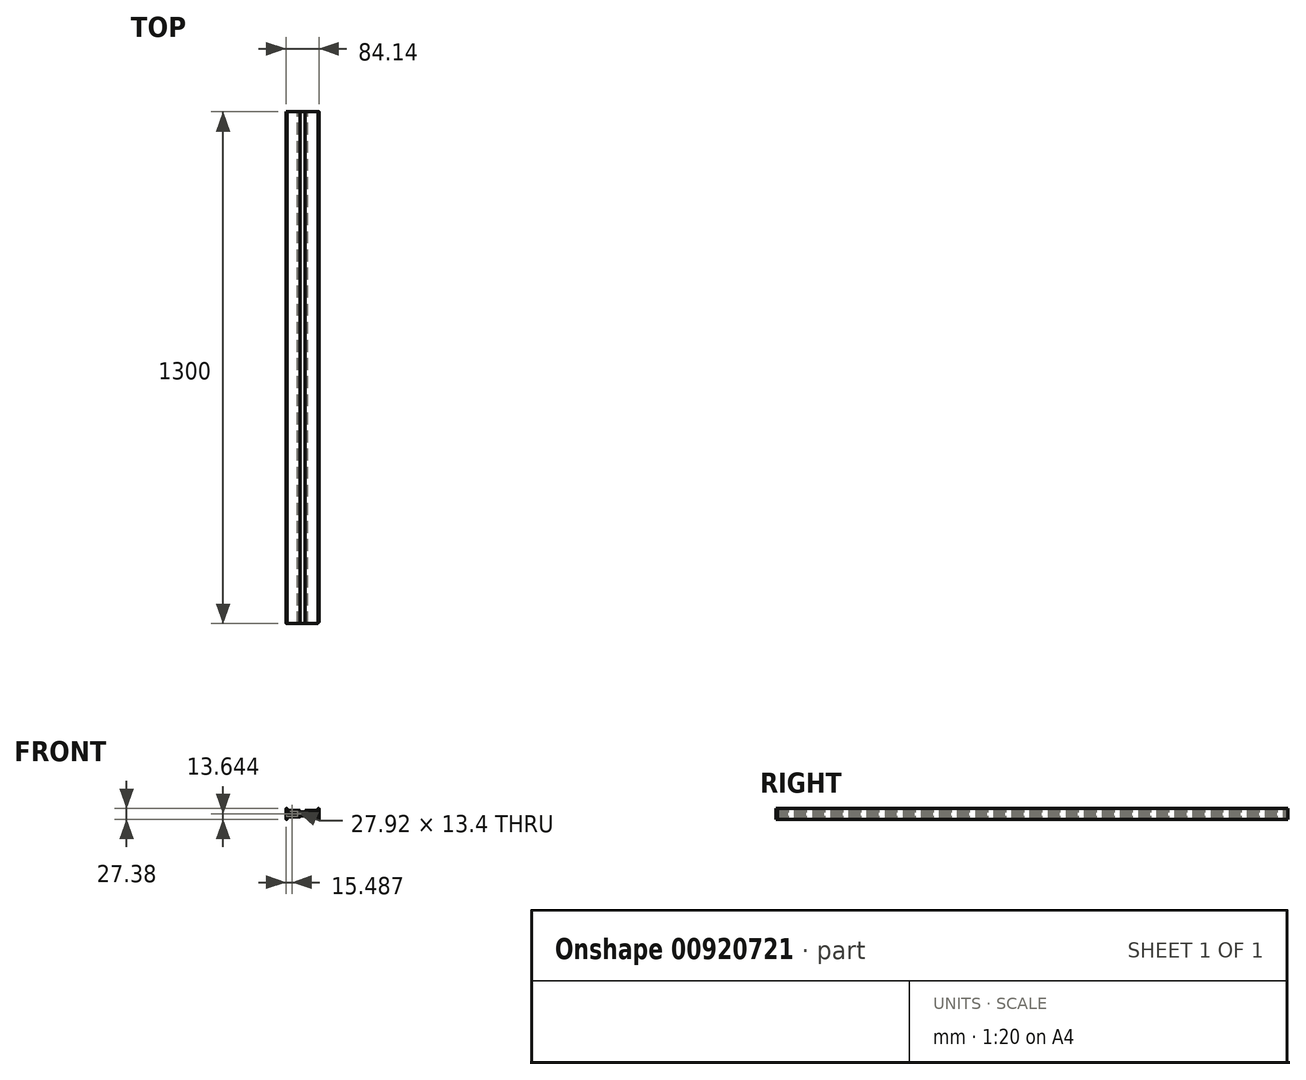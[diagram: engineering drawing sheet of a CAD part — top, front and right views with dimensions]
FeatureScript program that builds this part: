
annotation { "Feature Type Name" : "Feature", "Feature Type Description" : "" }
export const myFeature = defineFeature(function(context is Context, id is Id, definition is map)
    precondition{}
    {
        {
            var Q0;
            Q0=qCreatedBy(makeId("Front.planeOp"),FACE);
            var sketch = newSketch(context, id + "F0", { "sketchPlane" : qUnion([Q0])});
            skLineSegment(sketch, "E0", {"start": v(1.56, 28.72) * mm, "end": v(1.56, 1.75) * mm});
            skLineSegment(sketch, "E1", {"start": v(1.77, 1.54) * mm, "end": v(4.38, 1.54) * mm});
            skLineSegment(sketch, "E2", {"start": v(4.6, 1.75) * mm, "end": v(4.6, 2.8) * mm});
            skLineSegment(sketch, "E3", {"start": v(4.38, 3.02) * mm, "end": v(3.3, 3.02) * mm});
            skLineSegment(sketch, "E4", {"start": v(3.09, 3.23) * mm, "end": v(3.09, 6.74) * mm});
            skLineSegment(sketch, "E5", {"start": v(3.3, 6.95) * mm, "end": v(36.72, 6.95) * mm});
            skLineSegment(sketch, "E6", {"start": v(36.9, 7.28) * mm, "end": v(35.41, 9.64) * mm});
            skLineSegment(sketch, "E7", {"start": v(35.13, 9.71) * mm, "end": v(33.3, 8.77) * mm});
            skLineSegment(sketch, "E8", {"start": v(33, 8.96) * mm, "end": v(33, 13.05) * mm});
            skLineSegment(sketch, "E9", {"start": v(33.32, 13.23) * mm, "end": v(35.15, 12.04) * mm});
            skLineSegment(sketch, "E10", {"start": v(35.33, 12.14) * mm, "end": v(35.33, 14.1) * mm});
            skLineSegment(sketch, "E11", {"start": v(35.27, 14.2) * mm, "end": v(34.06, 14.95) * mm});
            skLineSegment(sketch, "E12", {"start": v(34.04, 15.3) * mm, "end": v(35.28, 16.3) * mm});
            skLineSegment(sketch, "E13", {"start": v(35.33, 16.38) * mm, "end": v(35.33, 18.3) * mm});
            skLineSegment(sketch, "E14", {"start": v(35.16, 18.39) * mm, "end": v(33.6, 17.48) * mm});
            skLineSegment(sketch, "E15", {"start": v(33.53, 17.46) * mm, "end": v(33.1, 17.46) * mm});
            skLineSegment(sketch, "E16", {"start": v(33, 17.58) * mm, "end": v(33, 21.77) * mm});
            skLineSegment(sketch, "E17", {"start": v(33.17, 21.87) * mm, "end": v(35.23, 20.65) * mm});
            skLineSegment(sketch, "E18", {"start": v(35.39, 20.68) * mm, "end": v(37, 23.23) * mm});
            skLineSegment(sketch, "E19", {"start": v(36.9, 23.4) * mm, "end": v(3.2, 23.4) * mm});
            skLineSegment(sketch, "E20", {"start": v(3.09, 23.51) * mm, "end": v(3.09, 27.31) * mm});
            skLineSegment(sketch, "E21", {"start": v(3.2, 27.43) * mm, "end": v(4.49, 27.43) * mm});
            skLineSegment(sketch, "E22", {"start": v(4.6, 27.54) * mm, "end": v(4.6, 28.8) * mm});
            skLineSegment(sketch, "E23", {"start": v(4.49, 28.92) * mm, "end": v(1.74, 28.9) * mm});
            skPoint(sketch, "E24.visualSharp", {"position": v(1.56, 28.9) * mm});
            skArc(sketch, "E24.filletArc", {"start": v(1.74, 28.9) * mm, "mid": v(1.61, 28.85) * mm, "end": v(1.56, 28.72) * mm});
            skPoint(sketch, "E25.visualSharp", {"position": v(4.6, 28.92) * mm});
            skArc(sketch, "E25.filletArc", {"start": v(4.6, 28.8) * mm, "mid": v(4.57, 28.89) * mm, "end": v(4.49, 28.92) * mm});
            skPoint(sketch, "E26.visualSharp", {"position": v(4.6, 27.43) * mm});
            skArc(sketch, "E26.filletArc", {"start": v(4.49, 27.43) * mm, "mid": v(4.57, 27.46) * mm, "end": v(4.6, 27.54) * mm});
            skPoint(sketch, "E27.visualSharp", {"position": v(3.09, 27.43) * mm});
            skArc(sketch, "E27.filletArc", {"start": v(3.2, 27.43) * mm, "mid": v(3.12, 27.4) * mm, "end": v(3.09, 27.31) * mm});
            skPoint(sketch, "E28.visualSharp", {"position": v(3.09, 23.4) * mm});
            skArc(sketch, "E28.filletArc", {"start": v(3.09, 23.51) * mm, "mid": v(3.12, 23.43) * mm, "end": v(3.2, 23.4) * mm});
            skPoint(sketch, "E29.visualSharp", {"position": v(37.1, 23.4) * mm});
            skArc(sketch, "E29.filletArc", {"start": v(37, 23.23) * mm, "mid": v(37, 23.34) * mm, "end": v(36.9, 23.4) * mm});
            skPoint(sketch, "E30.visualSharp", {"position": v(35.33, 20.6) * mm});
            skArc(sketch, "E30.filletArc", {"start": v(35.23, 20.65) * mm, "mid": v(35.32, 20.63) * mm, "end": v(35.39, 20.68) * mm});
            skPoint(sketch, "E31.visualSharp", {"position": v(33, 21.97) * mm});
            skArc(sketch, "E31.filletArc", {"start": v(33.17, 21.87) * mm, "mid": v(33.05, 21.87) * mm, "end": v(33, 21.77) * mm});
            skPoint(sketch, "E32.visualSharp", {"position": v(33, 17.46) * mm});
            skArc(sketch, "E32.filletArc", {"start": v(33, 17.58) * mm, "mid": v(33.03, 17.5) * mm, "end": v(33.1, 17.46) * mm});
            skPoint(sketch, "E33.visualSharp", {"position": v(33.56, 17.46) * mm});
            skArc(sketch, "E33.filletArc", {"start": v(33.53, 17.46) * mm, "mid": v(33.56, 17.47) * mm, "end": v(33.6, 17.48) * mm});
            skPoint(sketch, "E34.visualSharp", {"position": v(35.33, 18.49) * mm});
            skArc(sketch, "E34.filletArc", {"start": v(35.33, 18.3) * mm, "mid": v(35.27, 18.39) * mm, "end": v(35.16, 18.39) * mm});
            skPoint(sketch, "E35.visualSharp", {"position": v(35.33, 16.33) * mm});
            skArc(sketch, "E35.filletArc", {"start": v(35.28, 16.3) * mm, "mid": v(35.31, 16.33) * mm, "end": v(35.33, 16.38) * mm});
            skPoint(sketch, "E36.visualSharp", {"position": v(33.8, 15.11) * mm});
            skArc(sketch, "E36.filletArc", {"start": v(34.04, 15.3) * mm, "mid": v(33.96, 15.12) * mm, "end": v(34.06, 14.95) * mm});
            skPoint(sketch, "E37.visualSharp", {"position": v(35.33, 14.16) * mm});
            skArc(sketch, "E37.filletArc", {"start": v(35.33, 14.1) * mm, "mid": v(35.31, 14.16) * mm, "end": v(35.27, 14.2) * mm});
            skPoint(sketch, "E38.visualSharp", {"position": v(35.33, 11.93) * mm});
            skArc(sketch, "E38.filletArc", {"start": v(35.15, 12.04) * mm, "mid": v(35.27, 12.04) * mm, "end": v(35.33, 12.14) * mm});
            skPoint(sketch, "E39.visualSharp", {"position": v(33, 13.45) * mm});
            skArc(sketch, "E39.filletArc", {"start": v(33.32, 13.23) * mm, "mid": v(33.1, 13.24) * mm, "end": v(33, 13.05) * mm});
            skPoint(sketch, "E40.visualSharp", {"position": v(33, 8.6) * mm});
            skArc(sketch, "E40.filletArc", {"start": v(33, 8.96) * mm, "mid": v(33.1, 8.78) * mm, "end": v(33.3, 8.77) * mm});
            skPoint(sketch, "E41.visualSharp", {"position": v(35.3, 9.8) * mm});
            skArc(sketch, "E41.filletArc", {"start": v(35.41, 9.64) * mm, "mid": v(35.29, 9.73) * mm, "end": v(35.13, 9.71) * mm});
            skPoint(sketch, "E42.visualSharp", {"position": v(37.1, 6.95) * mm});
            skArc(sketch, "E42.filletArc", {"start": v(36.72, 6.95) * mm, "mid": v(36.9, 7.06) * mm, "end": v(36.9, 7.28) * mm});
            skPoint(sketch, "E43.visualSharp", {"position": v(3.09, 6.95) * mm});
            skArc(sketch, "E43.filletArc", {"start": v(3.3, 6.95) * mm, "mid": v(3.15, 6.89) * mm, "end": v(3.09, 6.74) * mm});
            skPoint(sketch, "E44.visualSharp", {"position": v(3.09, 3.02) * mm});
            skArc(sketch, "E44.filletArc", {"start": v(3.09, 3.23) * mm, "mid": v(3.15, 3.08) * mm, "end": v(3.3, 3.02) * mm});
            skPoint(sketch, "E45.visualSharp", {"position": v(4.6, 3.02) * mm});
            skArc(sketch, "E45.filletArc", {"start": v(4.6, 2.8) * mm, "mid": v(4.53, 2.95) * mm, "end": v(4.38, 3.02) * mm});
            skPoint(sketch, "E46.visualSharp", {"position": v(4.6, 1.54) * mm});
            skArc(sketch, "E46.filletArc", {"start": v(4.38, 1.54) * mm, "mid": v(4.53, 1.6) * mm, "end": v(4.6, 1.75) * mm});
            skPoint(sketch, "E47.visualSharp", {"position": v(1.56, 1.54) * mm});
            skArc(sketch, "E47.filletArc", {"start": v(1.56, 1.75) * mm, "mid": v(1.62, 1.6) * mm, "end": v(1.77, 1.54) * mm});
            skLineSegment(sketch, "E48", {"start": v(3.09, 21.89) * mm, "end": v(31, 21.89) * mm});
            skLineSegment(sketch, "E49", {"start": v(31, 21.89) * mm, "end": v(31, 8.48) * mm});
            skLineSegment(sketch, "E50", {"start": v(31, 8.48) * mm, "end": v(3.09, 8.48) * mm});
            skLineSegment(sketch, "E51", {"start": v(3.09, 8.48) * mm, "end": v(3.09, 21.89) * mm});
            skLineSegment(sketch, "E52.MirrorCS", {"start": v(53.72, 17.46) * mm, "end": v(54.15, 17.46) * mm});
            skArc(sketch, "E53.MirrorCS", {"start": v(54.26, 17.58) * mm, "mid": v(54.23, 17.5) * mm, "end": v(54.15, 17.46) * mm});
            skArc(sketch, "E54.MirrorCS", {"start": v(53.72, 17.46) * mm, "mid": v(53.7, 17.47) * mm, "end": v(53.67, 17.48) * mm});
            skLineSegment(sketch, "E55.MirrorCS", {"start": v(84.06, 27.43) * mm, "end": v(82.77, 27.43) * mm});
            skArc(sketch, "E56.MirrorCS", {"start": v(82.65, 28.8) * mm, "mid": v(82.69, 28.89) * mm, "end": v(82.77, 28.92) * mm});
            skLineSegment(sketch, "E57.MirrorCS", {"start": v(82.65, 27.54) * mm, "end": v(82.65, 28.8) * mm});
            skArc(sketch, "E58.MirrorCS", {"start": v(51.93, 14.1) * mm, "mid": v(51.94, 14.16) * mm, "end": v(51.98, 14.2) * mm});
            skArc(sketch, "E59.MirrorCS", {"start": v(84.17, 3.23) * mm, "mid": v(84.1, 3.08) * mm, "end": v(83.96, 3.02) * mm});
            skArc(sketch, "E60.MirrorCS", {"start": v(82.77, 27.43) * mm, "mid": v(82.69, 27.46) * mm, "end": v(82.65, 27.54) * mm});
            skArc(sketch, "E61.MirrorCS", {"start": v(84.06, 27.43) * mm, "mid": v(84.14, 27.4) * mm, "end": v(84.17, 27.31) * mm});
            skArc(sketch, "E62.MirrorCS", {"start": v(52.02, 20.65) * mm, "mid": v(51.94, 20.63) * mm, "end": v(51.87, 20.68) * mm});
            skArc(sketch, "E63.MirrorCS", {"start": v(51.85, 9.64) * mm, "mid": v(51.97, 9.73) * mm, "end": v(52.12, 9.71) * mm});
            skArc(sketch, "E64.MirrorCS", {"start": v(53.93, 13.23) * mm, "mid": v(54.15, 13.24) * mm, "end": v(54.26, 13.05) * mm});
            skLineSegment(sketch, "E65.MirrorCS", {"start": v(82.87, 3.02) * mm, "end": v(83.96, 3.02) * mm});
            skArc(sketch, "E66.MirrorCS", {"start": v(53.21, 15.3) * mm, "mid": v(53.3, 15.12) * mm, "end": v(53.2, 14.95) * mm});
            skLineSegment(sketch, "E67.MirrorCS", {"start": v(51.98, 14.2) * mm, "end": v(53.2, 14.95) * mm});
            skLineSegment(sketch, "E68.MirrorCS", {"start": v(52.1, 18.39) * mm, "end": v(53.67, 17.48) * mm});
            skArc(sketch, "E69.MirrorCS", {"start": v(83.96, 6.95) * mm, "mid": v(84.1, 6.89) * mm, "end": v(84.17, 6.74) * mm});
            skLineSegment(sketch, "E70.MirrorCS", {"start": v(53.93, 13.23) * mm, "end": v(52.1, 12.04) * mm});
            skArc(sketch, "E71.MirrorCS", {"start": v(84.17, 23.51) * mm, "mid": v(84.14, 23.43) * mm, "end": v(84.06, 23.4) * mm});
            skArc(sketch, "E72.MirrorCS", {"start": v(50.53, 6.95) * mm, "mid": v(50.35, 7.06) * mm, "end": v(50.35, 7.28) * mm});
            skArc(sketch, "E73.MirrorCS", {"start": v(51.97, 16.3) * mm, "mid": v(51.94, 16.33) * mm, "end": v(51.93, 16.38) * mm});
            skArc(sketch, "E74.MirrorCS", {"start": v(52.1, 12.04) * mm, "mid": v(51.99, 12.04) * mm, "end": v(51.93, 12.14) * mm});
            skLineSegment(sketch, "E75.MirrorCS", {"start": v(51.93, 16.38) * mm, "end": v(51.93, 18.3) * mm});
            skLineSegment(sketch, "E76.MirrorCS", {"start": v(53.21, 15.3) * mm, "end": v(51.97, 16.3) * mm});
            skLineSegment(sketch, "E77.MirrorCS", {"start": v(54.1, 21.87) * mm, "end": v(52.02, 20.65) * mm});
            skArc(sketch, "E78.MirrorCS", {"start": v(54.1, 21.87) * mm, "mid": v(54.2, 21.87) * mm, "end": v(54.26, 21.77) * mm});
            skArc(sketch, "E79.MirrorCS", {"start": v(50.26, 23.23) * mm, "mid": v(50.25, 23.34) * mm, "end": v(50.35, 23.4) * mm});
            skLineSegment(sketch, "E80.MirrorCS", {"start": v(82.66, 1.75) * mm, "end": v(82.66, 2.8) * mm});
            skArc(sketch, "E81.MirrorCS", {"start": v(82.87, 1.54) * mm, "mid": v(82.72, 1.6) * mm, "end": v(82.66, 1.75) * mm});
            skArc(sketch, "E82.MirrorCS", {"start": v(82.66, 2.8) * mm, "mid": v(82.72, 2.95) * mm, "end": v(82.87, 3.02) * mm});
            skArc(sketch, "E83.MirrorCS", {"start": v(85.52, 28.9) * mm, "mid": v(85.65, 28.85) * mm, "end": v(85.7, 28.72) * mm});
            skArc(sketch, "E84.MirrorCS", {"start": v(51.93, 18.3) * mm, "mid": v(51.99, 18.39) * mm, "end": v(52.1, 18.39) * mm});
            skLineSegment(sketch, "E85.MirrorCS", {"start": v(51.93, 12.14) * mm, "end": v(51.93, 14.1) * mm});
            skArc(sketch, "E86.MirrorCS", {"start": v(54.26, 8.96) * mm, "mid": v(54.16, 8.78) * mm, "end": v(53.95, 8.77) * mm});
            skLineSegment(sketch, "E87.MirrorCS", {"start": v(52.12, 9.71) * mm, "end": v(53.95, 8.77) * mm});
            skArc(sketch, "E88.MirrorCS", {"start": v(85.7, 1.75) * mm, "mid": v(85.64, 1.6) * mm, "end": v(85.49, 1.54) * mm});
            skLineSegment(sketch, "E89.MirrorCS", {"start": v(50.35, 7.28) * mm, "end": v(51.85, 9.64) * mm});
            skPoint(sketch, "E90.MirrorP", {"position": v(51.93, 14.16) * mm});
            skPoint(sketch, "E91.MirrorP", {"position": v(53.45, 15.11) * mm});
            skLineSegment(sketch, "E92.MirrorCS", {"start": v(51.87, 20.68) * mm, "end": v(50.26, 23.23) * mm});
            skPoint(sketch, "E93.MirrorP", {"position": v(51.93, 16.33) * mm});
            skPoint(sketch, "E94.MirrorP", {"position": v(51.93, 20.6) * mm});
            skPoint(sketch, "E95.MirrorP", {"position": v(51.93, 18.49) * mm});
            skPoint(sketch, "E96.MirrorP", {"position": v(51.95, 9.8) * mm});
            skPoint(sketch, "E97.MirrorP", {"position": v(53.7, 17.46) * mm});
            skPoint(sketch, "E98.MirrorP", {"position": v(54.26, 13.45) * mm});
            skPoint(sketch, "E99.MirrorP", {"position": v(84.17, 23.4) * mm});
            skPoint(sketch, "E100.MirrorP", {"position": v(54.26, 8.6) * mm});
            skLineSegment(sketch, "E101.MirrorCS", {"start": v(54.26, 17.58) * mm, "end": v(54.26, 21.77) * mm});
            skPoint(sketch, "E102.MirrorP", {"position": v(51.93, 11.93) * mm});
            skLineSegment(sketch, "E103.MirrorCS", {"start": v(54.26, 8.96) * mm, "end": v(54.26, 13.05) * mm});
            skPoint(sketch, "E104.MirrorP", {"position": v(84.17, 3.02) * mm});
            skPoint(sketch, "E105.MirrorP", {"position": v(54.26, 17.46) * mm});
            skPoint(sketch, "E106.MirrorP", {"position": v(54.26, 21.97) * mm});
            skLineSegment(sketch, "E107.MirrorCS", {"start": v(84.17, 21.89) * mm, "end": v(56.25, 21.89) * mm});
            skPoint(sketch, "E108.MirrorP", {"position": v(50.15, 6.95) * mm});
            skLineSegment(sketch, "E109.MirrorCS", {"start": v(56.25, 21.89) * mm, "end": v(56.25, 8.48) * mm});
            skLineSegment(sketch, "E110.MirrorCS", {"start": v(83.96, 6.95) * mm, "end": v(50.53, 6.95) * mm});
            skLineSegment(sketch, "E111.MirrorCS", {"start": v(56.25, 8.48) * mm, "end": v(84.17, 8.48) * mm});
            skLineSegment(sketch, "E112.MirrorCS", {"start": v(84.17, 23.51) * mm, "end": v(84.17, 27.31) * mm});
            skPoint(sketch, "E113.MirrorP", {"position": v(84.17, 27.43) * mm});
            skLineSegment(sketch, "E114.MirrorCS", {"start": v(85.49, 1.54) * mm, "end": v(82.87, 1.54) * mm});
            skLineSegment(sketch, "E115.MirrorCS", {"start": v(82.77, 28.92) * mm, "end": v(85.52, 28.9) * mm});
            skLineSegment(sketch, "E116.MirrorCS", {"start": v(84.17, 3.23) * mm, "end": v(84.17, 6.74) * mm});
            skPoint(sketch, "E117.MirrorP", {"position": v(50.15, 23.4) * mm});
            skLineSegment(sketch, "E118.MirrorCS", {"start": v(85.7, 28.72) * mm, "end": v(85.7, 1.75) * mm});
            skPoint(sketch, "E119.MirrorP", {"position": v(82.65, 27.43) * mm});
            skLineSegment(sketch, "E120.MirrorCS", {"start": v(50.35, 23.4) * mm, "end": v(84.06, 23.4) * mm});
            skPoint(sketch, "E121.MirrorP", {"position": v(82.66, 1.54) * mm});
            skLineSegment(sketch, "E122.MirrorCS", {"start": v(84.17, 8.48) * mm, "end": v(84.17, 21.89) * mm});
            skPoint(sketch, "E123.MirrorP", {"position": v(82.66, 3.02) * mm});
            skPoint(sketch, "E124.MirrorP", {"position": v(82.65, 28.92) * mm});
            skPoint(sketch, "E125.MirrorP", {"position": v(84.17, 6.95) * mm});
            skPoint(sketch, "E126.MirrorP", {"position": v(85.7, 28.9) * mm});
            skPoint(sketch, "E127.MirrorP", {"position": v(85.7, 1.54) * mm});
            skLineSegment(sketch, "E128", {"start": v(33.2, 21.62) * mm, "end": v(35.36, 20.35) * mm});
            skLineSegment(sketch, "E129", {"start": v(35.36, 20.35) * mm, "end": v(51.93, 20.35) * mm});
            skLineSegment(sketch, "E130", {"start": v(51.93, 20.35) * mm, "end": v(54.09, 21.62) * mm});
            skLineSegment(sketch, "E131", {"start": v(54.09, 21.62) * mm, "end": v(54.09, 17.69) * mm});
            skLineSegment(sketch, "E132", {"start": v(54.09, 17.69) * mm, "end": v(53.7, 17.69) * mm});
            skLineSegment(sketch, "E133", {"start": v(53.7, 17.69) * mm, "end": v(51.93, 18.58) * mm});
            skLineSegment(sketch, "E134", {"start": v(51.93, 18.58) * mm, "end": v(35.36, 18.58) * mm});
            skLineSegment(sketch, "E135", {"start": v(35.36, 18.58) * mm, "end": v(33.66, 17.58) * mm});
            skLineSegment(sketch, "E136", {"start": v(33.66, 17.58) * mm, "end": v(33.2, 17.58) * mm});
            skLineSegment(sketch, "E137", {"start": v(33.2, 17.58) * mm, "end": v(33.2, 21.62) * mm});
            skLineSegment(sketch, "E138.MirrorCS", {"start": v(35.33, 10.11) * mm, "end": v(51.9, 10.11) * mm});
            skLineSegment(sketch, "E139.MirrorCS", {"start": v(33.16, 12.89) * mm, "end": v(33.16, 8.84) * mm});
            skLineSegment(sketch, "E140.MirrorCS", {"start": v(33.63, 12.89) * mm, "end": v(33.16, 12.89) * mm});
            skLineSegment(sketch, "E141.MirrorCS", {"start": v(35.33, 11.88) * mm, "end": v(33.63, 12.89) * mm});
            skLineSegment(sketch, "E142.MirrorCS", {"start": v(51.9, 11.88) * mm, "end": v(35.33, 11.88) * mm});
            skLineSegment(sketch, "E143.MirrorCS", {"start": v(53.67, 12.78) * mm, "end": v(51.9, 11.88) * mm});
            skLineSegment(sketch, "E144.MirrorCS", {"start": v(54.06, 12.78) * mm, "end": v(53.67, 12.78) * mm});
            skLineSegment(sketch, "E145.MirrorCS", {"start": v(54.06, 8.84) * mm, "end": v(54.06, 12.78) * mm});
            skLineSegment(sketch, "E146.MirrorCS", {"start": v(51.9, 10.11) * mm, "end": v(54.06, 8.84) * mm});
            skLineSegment(sketch, "E147.MirrorCS", {"start": v(33.16, 8.84) * mm, "end": v(35.33, 10.11) * mm});
            skSolve(sketch);
        }
        {
            var Q0;
            Q0=makeQuery(id+"F0.imprint","IMPRINT",FACE,{"disambiguationData":[TD([[makeQuery(id+"F0.imprint","IMPRINT",EDGE,{"derivedFrom":sQuery(id+"F0.wireOp",EDGE,"E138.MirrorCS")}),1.0]])]});
            var Q1;
            Q1=makeQuery(id+"F0.imprint","IMPRINT",FACE,{"disambiguationData":[TD([[makeQuery(id+"F0.imprint","IMPRINT",EDGE,{"derivedFrom":sQuery(id+"F0.wireOp",EDGE,"E0")}),1.0]])]});
            var Q2;
            Q2=makeQuery(id+"F0.imprint","IMPRINT",FACE,{"disambiguationData":[TD([[makeQuery(id+"F0.imprint","IMPRINT",EDGE,{"derivedFrom":sQuery(id+"F0.wireOp",EDGE,"E52.MirrorCS")}),-1.0]])]});
            var Q3;
            Q3=makeQuery(id+"F0.imprint","IMPRINT",FACE,{"disambiguationData":[TD([[makeQuery(id+"F0.imprint","IMPRINT",EDGE,{"derivedFrom":sQuery(id+"F0.wireOp",EDGE,"E128")}),-1.0]])]});
            extrude(context, id + "F1", {"entities" : qUnion([Q0, Q1, Q2, Q3]), "depth" : 1300 * mm, "offsetDistance" : 25 * mm});
        }
        {
            var Q0;
            Q0=makeQuery(id+"F1.opExtrude","CAP_FACE",FACE,{"disambiguationData":[OSD([sQuery(id+"F0.wireOp",EDGE,"E52.MirrorCS"),sQuery(id+"F0.wireOp",EDGE,"E53.MirrorCS"),sQuery(id+"F0.wireOp",EDGE,"E54.MirrorCS"),sQuery(id+"F0.wireOp",EDGE,"E55.MirrorCS"),sQuery(id+"F0.wireOp",EDGE,"E56.MirrorCS"),sQuery(id+"F0.wireOp",EDGE,"E57.MirrorCS"),sQuery(id+"F0.wireOp",EDGE,"E58.MirrorCS"),sQuery(id+"F0.wireOp",EDGE,"E59.MirrorCS"),sQuery(id+"F0.wireOp",EDGE,"E60.MirrorCS"),sQuery(id+"F0.wireOp",EDGE,"E61.MirrorCS"),sQuery(id+"F0.wireOp",EDGE,"E62.MirrorCS"),sQuery(id+"F0.wireOp",EDGE,"E63.MirrorCS"),sQuery(id+"F0.wireOp",EDGE,"E64.MirrorCS"),sQuery(id+"F0.wireOp",EDGE,"E65.MirrorCS"),sQuery(id+"F0.wireOp",EDGE,"E66.MirrorCS"),sQuery(id+"F0.wireOp",EDGE,"E67.MirrorCS"),sQuery(id+"F0.wireOp",EDGE,"E68.MirrorCS"),sQuery(id+"F0.wireOp",EDGE,"E69.MirrorCS"),sQuery(id+"F0.wireOp",EDGE,"E70.MirrorCS"),sQuery(id+"F0.wireOp",EDGE,"E71.MirrorCS"),sQuery(id+"F0.wireOp",EDGE,"E72.MirrorCS"),sQuery(id+"F0.wireOp",EDGE,"E73.MirrorCS"),sQuery(id+"F0.wireOp",EDGE,"E74.MirrorCS"),sQuery(id+"F0.wireOp",EDGE,"E75.MirrorCS"),sQuery(id+"F0.wireOp",EDGE,"E76.MirrorCS"),sQuery(id+"F0.wireOp",EDGE,"E77.MirrorCS"),sQuery(id+"F0.wireOp",EDGE,"E78.MirrorCS"),sQuery(id+"F0.wireOp",EDGE,"E79.MirrorCS"),sQuery(id+"F0.wireOp",EDGE,"E80.MirrorCS"),sQuery(id+"F0.wireOp",EDGE,"E81.MirrorCS"),sQuery(id+"F0.wireOp",EDGE,"E82.MirrorCS"),sQuery(id+"F0.wireOp",EDGE,"E83.MirrorCS"),sQuery(id+"F0.wireOp",EDGE,"E84.MirrorCS"),sQuery(id+"F0.wireOp",EDGE,"E85.MirrorCS"),sQuery(id+"F0.wireOp",EDGE,"E86.MirrorCS"),sQuery(id+"F0.wireOp",EDGE,"E87.MirrorCS"),sQuery(id+"F0.wireOp",EDGE,"E88.MirrorCS"),sQuery(id+"F0.wireOp",EDGE,"E89.MirrorCS"),sQuery(id+"F0.wireOp",EDGE,"E92.MirrorCS"),sQuery(id+"F0.wireOp",EDGE,"E101.MirrorCS"),sQuery(id+"F0.wireOp",EDGE,"E103.MirrorCS"),sQuery(id+"F0.wireOp",EDGE,"E107.MirrorCS"),sQuery(id+"F0.wireOp",EDGE,"E109.MirrorCS"),sQuery(id+"F0.wireOp",EDGE,"E110.MirrorCS"),sQuery(id+"F0.wireOp",EDGE,"E111.MirrorCS"),sQuery(id+"F0.wireOp",EDGE,"E112.MirrorCS"),sQuery(id+"F0.wireOp",EDGE,"E114.MirrorCS"),sQuery(id+"F0.wireOp",EDGE,"E115.MirrorCS"),sQuery(id+"F0.wireOp",EDGE,"E116.MirrorCS"),sQuery(id+"F0.wireOp",EDGE,"E118.MirrorCS"),sQuery(id+"F0.wireOp",EDGE,"E120.MirrorCS"),sQuery(id+"F0.wireOp",EDGE,"E122.MirrorCS")])],"isStart":false});
            var sketch = newSketch(context, id + "F2", { "sketchPlane" : qUnion([Q0])});
            skLineSegment(sketch, "E148", {"start": v(82.65, 23.4) * mm, "end": v(82.65, 21.89) * mm});
            skLineSegment(sketch, "E149", {"start": v(82.65, 8.48) * mm, "end": v(82.65, 6.95) * mm});
            skSolve(sketch);
        }
        {
            var Q0;
            {var subQ3=sQuery(id+"F2.wireOp",EDGE,"E148");Q0=makeQuery(id+"F2.imprint","IMPRINT",FACE,{"disambiguationData":[TD([[makeQuery(id+"F2.imprint","IMPRINT",EDGE,{"derivedFrom":subQ3}),1.0]])]});}
            extrude(context, id + "F3", {"entities" : qUnion([Q0]), "operationType" : NewBodyOperationType.REMOVE, "oppositeDirection" : true, "depth" : 3 * mm, "offsetDistance" : 25 * mm});
        }
    });
